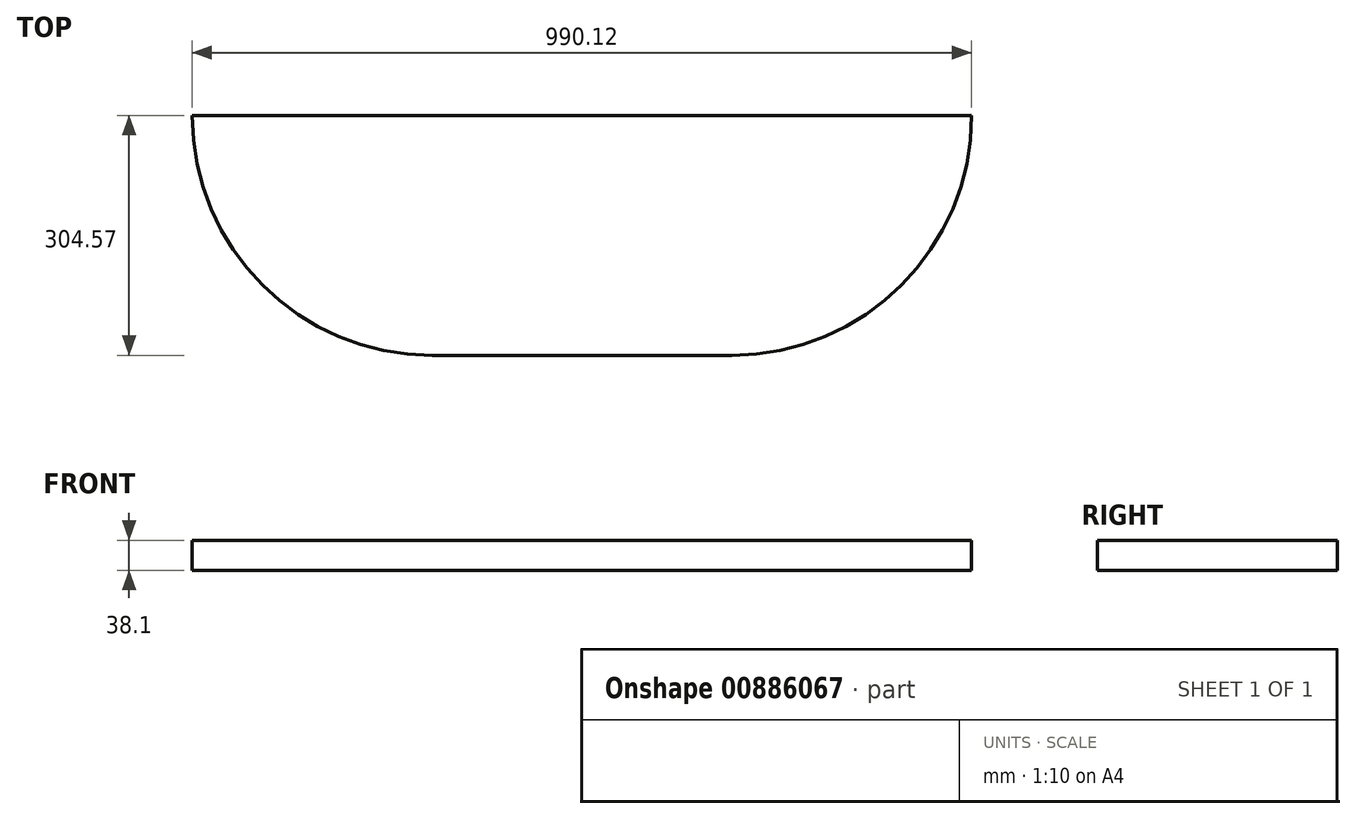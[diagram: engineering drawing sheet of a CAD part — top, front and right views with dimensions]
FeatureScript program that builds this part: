
annotation { "Feature Type Name" : "Feature", "Feature Type Description" : "" }
export const myFeature = defineFeature(function(context is Context, id is Id, definition is map)
    precondition{}
    {
        {
            var Q0;
            Q0=qCreatedBy(makeId("Top.planeOp"),FACE);
            var sketch = newSketch(context, id + "F0", { "sketchPlane" : qUnion([Q0])});
            skLineSegment(sketch, "E0", {"start": v(0, 0) * mm, "end": v(-190.5, 0) * mm});
            skLineSegment(sketch, "E1", {"start": v(-190.5, 0) * mm, "end": v(-495.3, 0) * mm});
            skLineSegment(sketch, "E2", {"start": v(0, 0) * mm, "end": v(190.5, 0) * mm});
            skLineSegment(sketch, "E3", {"start": v(190.5, 0) * mm, "end": v(495.3, 0) * mm});
            skArc(sketch, "E4", {"start": v(190.5, -304.55) * mm, "mid": v(405.85, -215.35) * mm, "end": v(495.05, 0) * mm});
            skArc(sketch, "E5", {"start": v(-190.5, -304.57) * mm, "mid": v(-405.94, -215.28) * mm, "end": v(-495.07, 0.23) * mm});
            skLineSegment(sketch, "E6", {"start": v(-190.5, -304.57) * mm, "end": v(190.5, -304.55) * mm});
            skSolve(sketch);
        }
        {
            var Q0;
            {var subQ4=sQuery(id+"F0.wireOp",EDGE,"E0");Q0=makeQuery(id+"F0.imprint","IMPRINT",FACE,{"disambiguationData":[TD([[makeQuery(id+"F0.imprint","IMPRINT",EDGE,{"derivedFrom":subQ4}),1.0]])]});}
            var Q1;
            Q1 = qSketchRegion(id + "F0", true);
            extrude(context, id + "F1", {"entities" : qUnion([Q0, Q1]), "depth" : 38.1 * mm, "offsetDistance" : 25.4 * mm});
        }
    });
